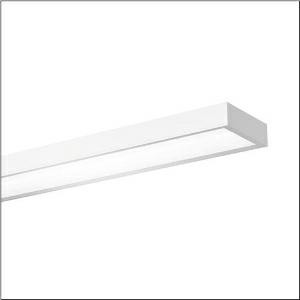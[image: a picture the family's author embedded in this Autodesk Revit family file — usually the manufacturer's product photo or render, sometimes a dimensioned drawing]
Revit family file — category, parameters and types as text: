
# Revit family: sport_31_51hs12dc4eca
name_source: partatom
category: Lighting Fixtures
units: mm (PartAtom-declared; Revit-internal decimal feet)

## family parameters
Cut with Voids When Loaded = No
Host = Face
Light Source = No
Part Type = Normal
Room Calculation Point = No
Round Connector Dimension = Use Diameter
Shared = No

## types (1)
- --- (1 x LED, 11990 lm, 89.4 W, 4000K)
    Apparent Load = 89 VA
    CIE Flux Codes = 65 89 97 100 100
    Color Rendering = 80
    Color Temperature = 4000K
    Default Elevation = 1800 mm
    Description = Sport 31, LED high bay luminaire, primary light control with reflector, of sheet steel, primary anti-glare with prismatic structure, of PC, primary optical cover: cover panel, of PC, light emission: direct distribution, primary light characteristic: symmetric, installation type: suspended mounting, recessed, surface-mounted, LED, rated luminous flux: 12.000lm, luminous efficacy: 137lm/W, light colour: 840, colour temperature: 4000K, control gear: DALI 2, with terminal, 5-pole, max. 2.5mm², mains connection: 220..240V, AC/DC, 50/60Hz, rated input power: 88W, housing, of sheet steel, traffic white (RAL 9016), length: 1.540mm, width: 315mm, height: 95mm, protection rating (complete): IP20, protection rating (lamp compartment, on room side): IP50, insulation class (complete): insulation class I (protective earthing), certification: CE, ENEC, UKCA, ball protection: ball impact resistant with ceiling mounting or chain suspension, impact resistance: IK08, permissible operating ambient temperature: -20..+35°C, standard: DIN 18032-3, EN 60598-2-22, packaging unit: 1 piece
    Height = 100 mm  [stored 0.328084 ft]
    Lamp = 1 x LED
    Lamp Light Flux = 11990 lm
    Lamp Power = 89.4 W
    Lamp count = 1
    Length = 1500 mm
    Luminous efficacy = 134 lm/W
    Manufacturer = Siteco
    ModVariant = No
    Model = 51HS12DC4ECA
    Mounting Place = Ceiling
    Mounting Type = Pendant
    Number of Poles = 1
    OnlyDefault = Yes
    Power Factor = 1
    Product Name = Sport 31
    Product group = LED high bay luminaire
    ProductGroupID = 903
    Protection Class = Protection class I
    Protection Degree = IP 20
    RLX_Detail_Level = 1
    RLX_Emergency_Light_Flux = 0 lm
    RLX_Emergency_Type = 0
    RLX_Emergency_Type_DB = No
    RlxData = <blob elided: 22785 chars, md5=ebce017d>
    Socket = socket
    Standby Power = 0 W
    System Light Flux = 11990 lm
    System Power = 89 W
    Type Comments = factory setting: luminous flux: 100 % | dim-lin: 254 | 380 mA
    Type Image = l_1006823.jpg
    URL = http://relux.com
    VarID = @adj_197178
    Voltage = 0 V
    Weight = 0.00 kg
    Width = 315 mm

note: [stored X ft] marks values corroborated as IEEE doubles in the binary element streams (Revit-internal decimal feet)

## geometry (parser evidence)
native form markers: Blend x4, Sweep x10
no freeform markers — native parametric forms only
